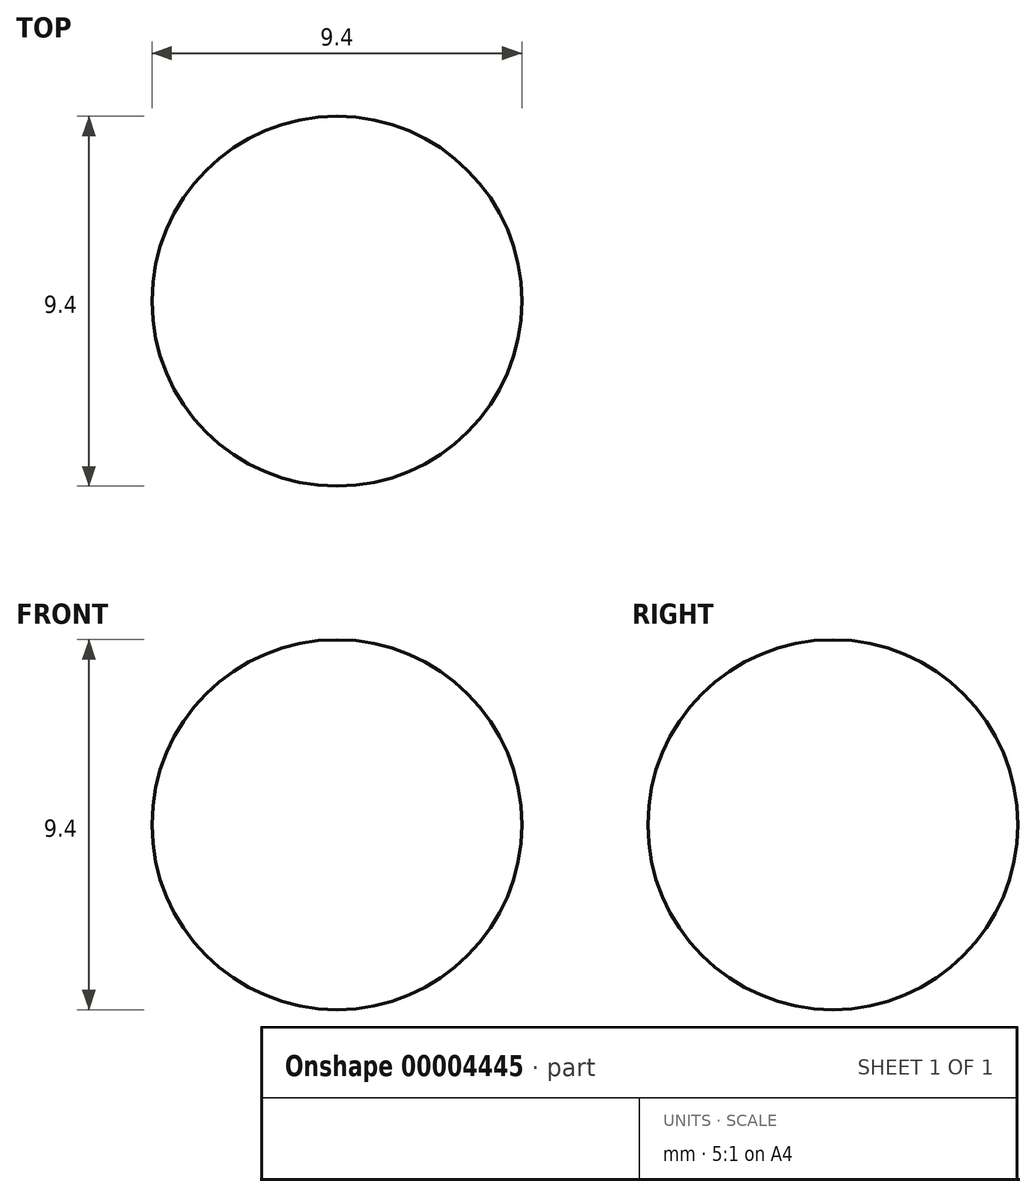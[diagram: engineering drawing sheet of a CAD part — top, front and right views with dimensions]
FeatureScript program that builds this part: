
annotation { "Feature Type Name" : "Feature", "Feature Type Description" : "" }
export const myFeature = defineFeature(function(context is Context, id is Id, definition is map)
    precondition{}
    {
        {
            var Q0;
            Q0=qCreatedBy(makeId("Front.planeOp"),FACE);
            var sketch = newSketch(context, id + "F0", { "sketchPlane" : qUnion([Q0])});
            skCircle(sketch, "E0", {"center": v(0, 0) * mm, "radius": 4.7 * mm});
            skLineSegment(sketch, "E1", {"start": v(0, 4.7) * mm, "end": v(0, -4.7) * mm});
            skSolve(sketch);
        }
        {
            var Q0;
            {var subQ0=sQuery(id+"F0.wireOp",EDGE,"E1");Q0=makeQuery(id+"F0.imprint","IMPRINT",FACE,{"disambiguationData":[TD([[makeQuery(id+"F0.imprint","IMPRINT",EDGE,{"derivedFrom":subQ0}),1.0]])]});}
            var Q1;
            Q1=sQuery(id+"F0.wireOp",EDGE,"E1");
            revolve(context, id + "F1", {"entities" : qUnion([Q0]), "axis" : qUnion([Q1]), "revolveType" : RevolveType.FULL});
        }
    });
